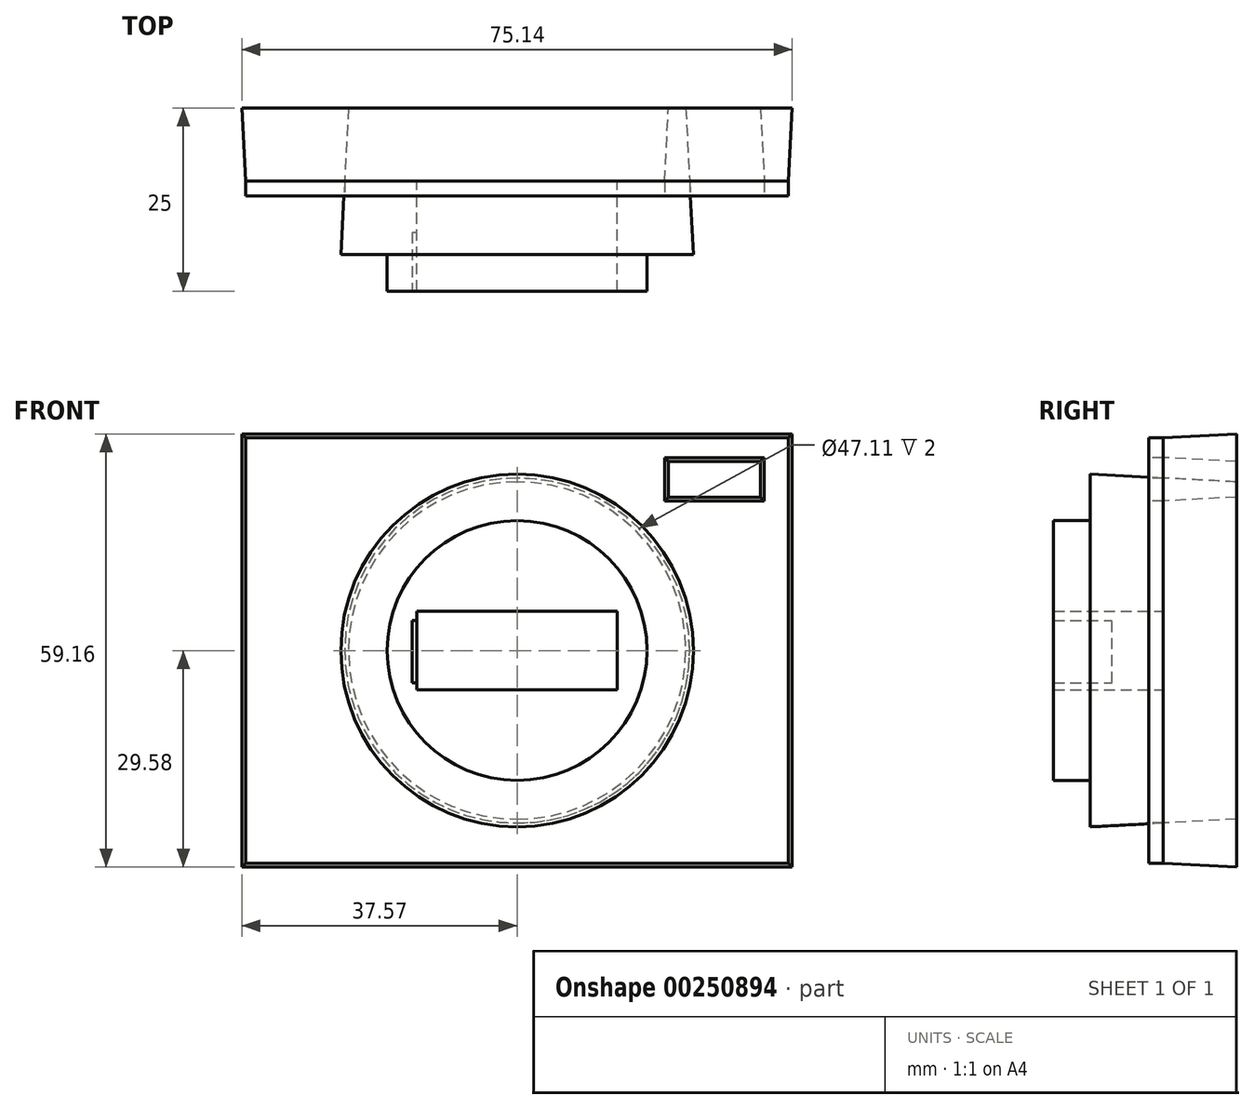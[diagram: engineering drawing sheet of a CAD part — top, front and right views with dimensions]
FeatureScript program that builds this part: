
annotation { "Feature Type Name" : "Feature", "Feature Type Description" : "" }
export const myFeature = defineFeature(function(context is Context, id is Id, definition is map)
    precondition{}
    {
        {
            var Q0;
            Q0=qCreatedBy(makeId("Front.planeOp"),FACE);
            var sketch = newSketch(context, id + "F0", { "sketchPlane" : qUnion([Q0])});
            skLineSegment(sketch, "E0.bottom", {"start": v(37.05, -29.05) * mm, "end": v(-37.05, -29.05) * mm});
            skLineSegment(sketch, "E0.top", {"start": v(37.05, 29.05) * mm, "end": v(-37.05, 29.05) * mm});
            skLineSegment(sketch, "E0.left", {"start": v(37.05, -29.05) * mm, "end": v(37.05, 29.05) * mm});
            skLineSegment(sketch, "E0.right", {"start": v(-37.05, -29.05) * mm, "end": v(-37.05, 29.05) * mm});
            skPoint(sketch, "E0.middle", {"position": v(0, 0) * mm});
            skCircle(sketch, "E1", {"center": v(0, 0) * mm, "radius": 23.55 * mm});
            skCircle(sketch, "E2", {"center": v(0, 0) * mm, "radius": 17.74 * mm});
            skLineSegment(sketch, "E3.bottom", {"start": v(-13.7, -5.38) * mm, "end": v(13.7, -5.38) * mm});
            skLineSegment(sketch, "E3.top", {"start": v(-13.7, 5.38) * mm, "end": v(13.7, 5.38) * mm});
            skLineSegment(sketch, "E3.left", {"start": v(-13.7, -5.38) * mm, "end": v(-13.7, 5.38) * mm});
            skLineSegment(sketch, "E3.right", {"start": v(13.7, -5.38) * mm, "end": v(13.7, 5.38) * mm});
            skLineSegment(sketch, "E4.bottom", {"start": v(33.75, 20.43) * mm, "end": v(20.13, 20.43) * mm});
            skLineSegment(sketch, "E4.top", {"start": v(33.75, 26.35) * mm, "end": v(20.13, 26.35) * mm});
            skLineSegment(sketch, "E4.left", {"start": v(33.75, 20.43) * mm, "end": v(33.75, 26.35) * mm});
            skLineSegment(sketch, "E4.right", {"start": v(20.13, 20.43) * mm, "end": v(20.13, 26.35) * mm});
            skPoint(sketch, "E4.middle", {"position": v(26.94, 23.39) * mm});
            skSolve(sketch);
        }
        {
            var Q0;
            Q0=makeQuery(id+"F0.imprint","IMPRINT",FACE,{"disambiguationData":[TD([[makeQuery(id+"F0.imprint","IMPRINT",EDGE,{"derivedFrom":sQuery(id+"F0.wireOp",EDGE,"E0.bottom")}),-1.0]])]});
            var Q1;
            Q1=sQuery(id+"F0.wireOp",EDGE,"E0.top");
            var Q2;
            Q2=sQuery(id+"F0.wireOp",EDGE,"E0.right");
            var Q3;
            Q3=sQuery(id+"F0.wireOp",EDGE,"E0.bottom");
            var Q4;
            Q4=sQuery(id+"F0.wireOp",EDGE,"E0.left");
            extrude(context, id + "F1", {"entities" : qUnion([Q0]), "surfaceEntities" : qUnion([Q1, Q2, Q3, Q4]), "oppositeDirection" : true, "depth" : 10 * mm, "hasDraft" : true, "draftAngle" : 3 * degree, "hasSecondDirection" : true, "secondDirectionOppositeDirection" : false, "secondDirectionDepth" : 2 * mm});
        }
        {
            var Q0;
            Q0=makeQuery(id+"F0.imprint","IMPRINT",FACE,{"disambiguationData":[TD([[makeQuery(id+"F0.imprint","IMPRINT",EDGE,{"derivedFrom":sQuery(id+"F0.wireOp",EDGE,"E1")}),1.0]])]});
            extrude(context, id + "F2", {"entities" : qUnion([Q0]), "depth" : 10 * mm, "hasDraft" : true, "draftAngle" : 3 * degree});
        }
        {
            var Q0;
            Q0=makeQuery(id+"F0.imprint","IMPRINT",FACE,{"disambiguationData":[TD([[makeQuery(id+"F0.imprint","IMPRINT",EDGE,{"derivedFrom":sQuery(id+"F0.wireOp",EDGE,"E2")}),1.0]])]});
            var Q1;
            Q1=sQuery(id+"F0.wireOp",EDGE,"E2");
            extrude(context, id + "F3", {"entities" : qUnion([Q0]), "operationType" : NewBodyOperationType.ADD, "surfaceEntities" : qUnion([Q1]), "depth" : 15 * mm});
        }
        {
            var Q0;
            Q0=makeQuery(id+"F3.opExtrude","CAP_FACE",FACE,{"disambiguationData":[OSD([sQuery(id+"F0.wireOp",EDGE,"E2")])],"isStart":false});
            var sketch = newSketch(context, id + "F4", { "sketchPlane" : qUnion([Q0])});
            skLineSegment(sketch, "E5.bottom", {"start": v(13.04, -4.4) * mm, "end": v(-14.35, -4.4) * mm});
            skLineSegment(sketch, "E5.top", {"start": v(13.04, 4.08) * mm, "end": v(-14.35, 4.08) * mm});
            skLineSegment(sketch, "E5.left", {"start": v(13.04, -4.4) * mm, "end": v(13.04, 4.08) * mm});
            skLineSegment(sketch, "E5.right", {"start": v(-14.35, -4.4) * mm, "end": v(-14.35, 4.08) * mm});
            skPoint(sketch, "E5.middle", {"position": v(-0.65, -0.16) * mm});
            skSolve(sketch);
        }
        {
            var Q0;
            Q0=makeQuery(id+"F4.imprint","IMPRINT",FACE,{"disambiguationData":[TD([[makeQuery(id+"F4.imprint","IMPRINT",EDGE,{"derivedFrom":sQuery(id+"F4.wireOp",EDGE,"E5.bottom")}),-1.0]])]});
            extrude(context, id + "F5", {"entities" : qUnion([Q0]), "operationType" : NewBodyOperationType.REMOVE, "oppositeDirection" : true, "depth" : 8 * mm});
        }
    });
